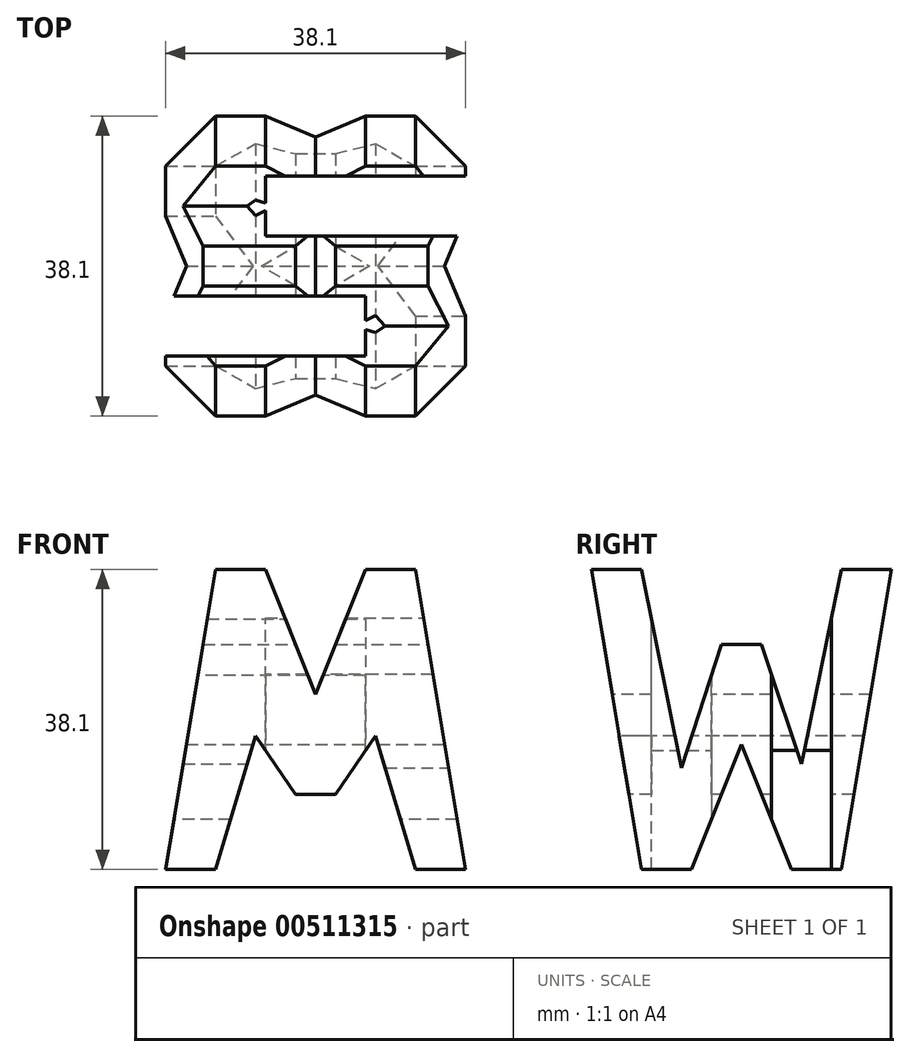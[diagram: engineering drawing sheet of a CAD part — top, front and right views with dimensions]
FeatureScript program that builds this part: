
annotation { "Feature Type Name" : "Feature", "Feature Type Description" : "" }
export const myFeature = defineFeature(function(context is Context, id is Id, definition is map)
    precondition{}
    {
        {
            var Q0;
            Q0=qCreatedBy(makeId("Front.planeOp"),FACE);
            var sketch = newSketch(context, id + "F0", { "sketchPlane" : qUnion([Q0])});
            skLineSegment(sketch, "E0", {"start": v(0, 0) * mm, "end": v(0, 38.1) * mm});
            skLineSegment(sketch, "E1", {"start": v(0, 38.1) * mm, "end": v(38.1, 38.1) * mm});
            skLineSegment(sketch, "E2", {"start": v(38.1, 38.1) * mm, "end": v(38.1, 0) * mm});
            skLineSegment(sketch, "E3", {"start": v(38.1, 0) * mm, "end": v(0, 0) * mm});
            skSolve(sketch);
        }
        {
            var Q0;
            Q0 = qSketchRegion(id + "F0", true);
            extrude(context, id + "F1", {"entities" : qUnion([Q0]), "depth" : 38.1 * mm, "offsetDistance" : 25.4 * mm});
        }
        {
            var Q0;
            Q0=qCreatedBy(makeId("Front.planeOp"),FACE);
            cPlane(context, id + "F2", {"entities" : qUnion([Q0]), "cplaneType" : CPlaneType.OFFSET, "offset" : 38.1 * mm, "width" : 152.4 * mm, "height" : 152.4 * mm});
        }
        {
            var Q0;
            Q0=qCreatedBy(makeId("Right.planeOp"),FACE);
            cPlane(context, id + "F3", {"entities" : qUnion([Q0]), "cplaneType" : CPlaneType.OFFSET, "offset" : 38.1 * mm, "width" : 152.4 * mm, "height" : 152.4 * mm});
        }
        {
            var Q0;
            Q0=qCreatedBy(makeId("Top.planeOp"),FACE);
            cPlane(context, id + "F4", {"entities" : qUnion([Q0]), "cplaneType" : CPlaneType.OFFSET, "offset" : 38.1 * mm, "width" : 152.4 * mm, "height" : 152.4 * mm});
        }
        {
            var Q0;
            Q0=qCreatedBy(id+"F3.planeOp",FACE);
            var sketch = newSketch(context, id + "F5", { "sketchPlane" : qUnion([Q0])});
            skLineSegment(sketch, "E4", {"start": v(0, 38.1) * mm, "end": v(-38.1, 38.1) * mm});
            skLineSegment(sketch, "E5", {"start": v(-38.1, 38.1) * mm, "end": v(-38.1, 0) * mm});
            skLineSegment(sketch, "E6", {"start": v(0, 0) * mm, "end": v(-38.1, 0) * mm});
            skLineSegment(sketch, "E7", {"start": v(-38.1, 38.1) * mm, "end": v(-31.75, 0) * mm});
            skLineSegment(sketch, "E8", {"start": v(-25.4, 0) * mm, "end": v(-19.05, 15.87) * mm});
            skLineSegment(sketch, "E9", {"start": v(-19.05, 15.87) * mm, "end": v(-12.7, 0) * mm});
            skLineSegment(sketch, "E10", {"start": v(0, 38.1) * mm, "end": v(-6.35, 0) * mm});
            skLineSegment(sketch, "E11", {"start": v(-31.75, 38.1) * mm, "end": v(-26.67, 12.89) * mm});
            skLineSegment(sketch, "E12", {"start": v(-26.67, 12.89) * mm, "end": v(-21.59, 28.57) * mm});
            skLineSegment(sketch, "E13", {"start": v(-21.59, 28.57) * mm, "end": v(-16.5, 28.57) * mm});
            skLineSegment(sketch, "E14", {"start": v(-16.5, 28.57) * mm, "end": v(-11.43, 13.4) * mm});
            skLineSegment(sketch, "E15", {"start": v(-11.43, 13.4) * mm, "end": v(-6.35, 38.1) * mm});
            skLineSegment(sketch, "E16", {"start": v(0, 38.1) * mm, "end": v(0, 0) * mm});
            skSolve(sketch);
        }
        {
            var Q0;
            {var subQ2=sQuery(id+"F5.wireOp",EDGE,"E10");Q0=makeQuery(id+"F5.imprint","IMPRINT",FACE,{"disambiguationData":[TD([[makeQuery(id+"F5.imprint","IMPRINT",EDGE,{"derivedFrom":subQ2}),1.0]])]});}
            var Q1;
            {var subQ0=sQuery(id+"F5.wireOp",EDGE,"E11");Q1=makeQuery(id+"F5.imprint","IMPRINT",FACE,{"disambiguationData":[TD([[makeQuery(id+"F5.imprint","IMPRINT",EDGE,{"derivedFrom":subQ0}),1.0]])]});}
            var Q2;
            {var subQ0=sQuery(id+"F5.wireOp",EDGE,"E8");Q2=makeQuery(id+"F5.imprint","IMPRINT",FACE,{"disambiguationData":[TD([[makeQuery(id+"F5.imprint","IMPRINT",EDGE,{"derivedFrom":subQ0}),-1.0]])]});}
            var Q3;
            {var subQ0=sQuery(id+"F5.wireOp",EDGE,"E5");Q3=makeQuery(id+"F5.imprint","IMPRINT",FACE,{"disambiguationData":[TD([[makeQuery(id+"F5.imprint","IMPRINT",EDGE,{"derivedFrom":subQ0}),1.0]])]});}
            extrude(context, id + "F6", {"entities" : qUnion([Q0, Q1, Q2, Q3]), "operationType" : NewBodyOperationType.REMOVE, "oppositeDirection" : true, "depth" : 38.1 * mm, "offsetDistance" : 25.4 * mm});
        }
        {
            var Q0;
            Q0=qCreatedBy(id+"F2.planeOp",FACE);
            var sketch = newSketch(context, id + "F7", { "sketchPlane" : qUnion([Q0])});
            skLineSegment(sketch, "E17", {"start": v(0, 0) * mm, "end": v(0, 38.1) * mm});
            skLineSegment(sketch, "E18", {"start": v(38.1, 38.1) * mm, "end": v(38.1, 0) * mm});
            skLineSegment(sketch, "E19", {"start": v(38.1, 0) * mm, "end": v(0, 0) * mm});
            skLineSegment(sketch, "E20", {"start": v(0, 0) * mm, "end": v(6.35, 38.1) * mm});
            skLineSegment(sketch, "E21", {"start": v(12.7, 38.1) * mm, "end": v(19.05, 22.23) * mm});
            skLineSegment(sketch, "E22", {"start": v(19.05, 22.23) * mm, "end": v(25.4, 38.15) * mm});
            skLineSegment(sketch, "E23", {"start": v(38.1, 0) * mm, "end": v(31.75, 38.1) * mm});
            skLineSegment(sketch, "E24", {"start": v(6.35, 38.1) * mm, "end": v(12.7, 38.1) * mm});
            skLineSegment(sketch, "E25", {"start": v(25.4, 38.15) * mm, "end": v(31.75, 38.1) * mm});
            skLineSegment(sketch, "E26", {"start": v(6.35, 0) * mm, "end": v(11.43, 16.97) * mm});
            skLineSegment(sketch, "E27", {"start": v(11.43, 16.97) * mm, "end": v(16.51, 9.53) * mm});
            skLineSegment(sketch, "E28", {"start": v(16.51, 9.53) * mm, "end": v(21.59, 9.53) * mm});
            skLineSegment(sketch, "E29", {"start": v(21.59, 9.53) * mm, "end": v(26.67, 16.97) * mm});
            skLineSegment(sketch, "E30", {"start": v(26.67, 16.97) * mm, "end": v(31.75, 0) * mm});
            skLineSegment(sketch, "E31", {"start": v(6.35, 38.1) * mm, "end": v(0, 38.1) * mm});
            skLineSegment(sketch, "E32", {"start": v(31.75, 38.1) * mm, "end": v(38.1, 38.1) * mm});
            skLineSegment(sketch, "E33", {"start": v(12.7, 38.1) * mm, "end": v(25.4, 38.15) * mm});
            skSolve(sketch);
        }
        {
            var Q0;
            Q0=makeQuery(id+"F7.imprint","IMPRINT",FACE,{"disambiguationData":[TD([[makeQuery(id+"F7.imprint","IMPRINT",EDGE,{"derivedFrom":sQuery(id+"F7.wireOp",EDGE,"E17")}),-1.0]])]});
            var Q1;
            Q1=makeQuery(id+"F7.imprint","IMPRINT",FACE,{"disambiguationData":[TD([[makeQuery(id+"F7.imprint","IMPRINT",EDGE,{"derivedFrom":sQuery(id+"F7.wireOp",EDGE,"E21")}),1.0]])]});
            var Q2;
            Q2=makeQuery(id+"F7.imprint","IMPRINT",FACE,{"disambiguationData":[TD([[makeQuery(id+"F7.imprint","IMPRINT",EDGE,{"derivedFrom":sQuery(id+"F7.wireOp",EDGE,"E18")}),-1.0]])]});
            var Q3;
            {var subQ0=sQuery(id+"F7.wireOp",EDGE,"E26");Q3=makeQuery(id+"F7.imprint","IMPRINT",FACE,{"disambiguationData":[TD([[makeQuery(id+"F7.imprint","IMPRINT",EDGE,{"derivedFrom":subQ0}),-1.0]])]});}
            extrude(context, id + "F8", {"entities" : qUnion([Q0, Q1, Q2, Q3]), "operationType" : NewBodyOperationType.REMOVE, "oppositeDirection" : true, "depth" : 38.1 * mm, "offsetDistance" : 25.4 * mm});
        }
        {
            var Q0;
            Q0=qCreatedBy(id+"F4.planeOp",FACE);
            var sketch = newSketch(context, id + "F9", { "sketchPlane" : qUnion([Q0])});
            skLineSegment(sketch, "E34", {"start": v(0, 0) * mm, "end": v(0, -38.1) * mm});
            skLineSegment(sketch, "E35", {"start": v(0, -38.1) * mm, "end": v(38.1, -38.1) * mm});
            skLineSegment(sketch, "E36", {"start": v(38.1, -38.1) * mm, "end": v(38.1, 0) * mm});
            skLineSegment(sketch, "E37", {"start": v(38.1, 0) * mm, "end": v(0, 0) * mm});
            skLineSegment(sketch, "E38", {"start": v(38.1, -7.62) * mm, "end": v(12.7, -7.62) * mm});
            skLineSegment(sketch, "E39", {"start": v(12.7, -7.62) * mm, "end": v(12.7, -15.24) * mm});
            skLineSegment(sketch, "E40", {"start": v(12.7, -15.24) * mm, "end": v(38.1, -15.24) * mm});
            skLineSegment(sketch, "E41", {"start": v(0, -22.86) * mm, "end": v(25.4, -22.86) * mm});
            skLineSegment(sketch, "E42", {"start": v(25.4, -22.86) * mm, "end": v(25.4, -30.48) * mm});
            skLineSegment(sketch, "E43", {"start": v(25.4, -30.48) * mm, "end": v(0, -30.48) * mm});
            skLineSegment(sketch, "E44", {"start": v(38.1, -7.62) * mm, "end": v(38.1, -15.24) * mm});
            skLineSegment(sketch, "E45", {"start": v(0, -22.86) * mm, "end": v(0, -30.48) * mm});
            skSolve(sketch);
        }
        {
            var Q0;
            Q0=makeQuery(id+"F9.imprint","IMPRINT",FACE,{"disambiguationData":[TD([[makeQuery(id+"F9.imprint","IMPRINT",EDGE,{"derivedFrom":sQuery(id+"F9.wireOp",EDGE,"E38")}),1.0]])]});
            var Q1;
            Q1=makeQuery(id+"F9.imprint","IMPRINT",FACE,{"disambiguationData":[TD([[makeQuery(id+"F9.imprint","IMPRINT",EDGE,{"derivedFrom":sQuery(id+"F9.wireOp",EDGE,"E41")}),-1.0]])]});
            extrude(context, id + "F10", {"entities" : qUnion([Q0, Q1]), "operationType" : NewBodyOperationType.REMOVE, "oppositeDirection" : true, "depth" : 38.1 * mm, "offsetDistance" : 25.4 * mm});
        }
    });
